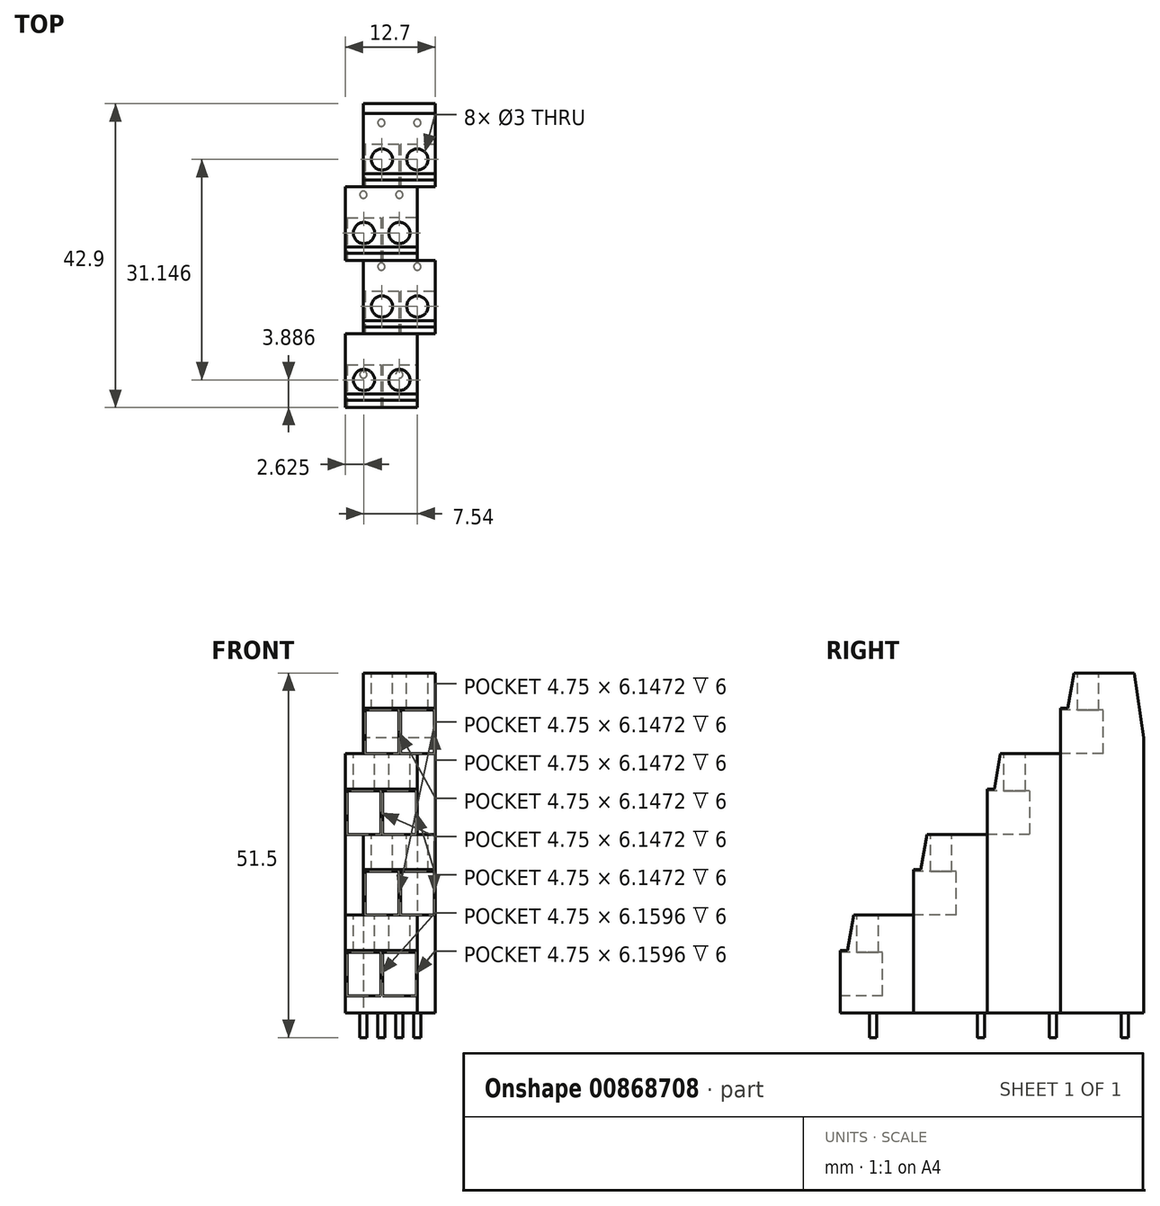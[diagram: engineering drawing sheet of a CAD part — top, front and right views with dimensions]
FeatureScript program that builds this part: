
annotation { "Feature Type Name" : "Feature", "Feature Type Description" : "" }
export const myFeature = defineFeature(function(context is Context, id is Id, definition is map)
    precondition{}
    {
        {
            var Q0;
            Q0=qCreatedBy(makeId("Right.planeOp"),FACE);
            var sketch = newSketch(context, id + "F0", { "sketchPlane" : qUnion([Q0])});
            skLineSegment(sketch, "E0.bottom", {"start": v(1.88, 24.08) * mm, "end": v(10.38, 24.08) * mm});
            skLineSegment(sketch, "E0.top", {"start": v(-31.15, -23.92) * mm, "end": v(11.75, -23.92) * mm});
            skLineSegment(sketch, "E0.left", {"start": v(-31.15, -15.12) * mm, "end": v(-31.15, -23.92) * mm});
            skLineSegment(sketch, "E0.right", {"start": v(11.75, 14.92) * mm, "end": v(11.75, -23.92) * mm});
            skPoint(sketch, "E0.middle", {"position": v(-0.86, 0) * mm});
            skLineSegment(sketch, "E1", {"start": v(-31.15, -15.12) * mm, "end": v(-30.15, -15.12) * mm});
            skLineSegment(sketch, "E2", {"start": v(-30.15, -15.12) * mm, "end": v(-29.26, -10.12) * mm});
            skLineSegment(sketch, "E3", {"start": v(-29.26, -10.12) * mm, "end": v(-20.76, -10.12) * mm});
            skLineSegment(sketch, "E4", {"start": v(-20.76, -10.12) * mm, "end": v(-20.76, -3.72) * mm});
            skLineSegment(sketch, "E5", {"start": v(-20.76, -3.72) * mm, "end": v(-19.76, -3.72) * mm});
            skLineSegment(sketch, "E6", {"start": v(-19.76, -3.72) * mm, "end": v(-18.88, 1.28) * mm});
            skLineSegment(sketch, "E7", {"start": v(-18.88, 1.28) * mm, "end": v(-10.38, 1.28) * mm});
            skLineSegment(sketch, "E8", {"start": v(-10.38, 1.28) * mm, "end": v(-10.38, 7.68) * mm});
            skLineSegment(sketch, "E9", {"start": v(-10.38, 7.68) * mm, "end": v(-9.38, 7.68) * mm});
            skLineSegment(sketch, "E10", {"start": v(-9.38, 7.68) * mm, "end": v(-8.5, 12.68) * mm});
            skLineSegment(sketch, "E11", {"start": v(-8.5, 12.68) * mm, "end": v(0, 12.68) * mm});
            skLineSegment(sketch, "E12", {"start": v(0, 12.68) * mm, "end": v(0, 19.08) * mm});
            skLineSegment(sketch, "E13", {"start": v(0, 19.08) * mm, "end": v(1, 19.08) * mm});
            skLineSegment(sketch, "E14", {"start": v(1, 19.08) * mm, "end": v(1.88, 24.08) * mm});
            skLineSegment(sketch, "E15", {"start": v(10.38, 24.08) * mm, "end": v(11.75, 14.92) * mm});
            skSolve(sketch);
        }
        {
            var Q0;
            Q0=qSketchRegion(id+"F0",true);
            extrude(context, id + "F1", {"entities" : qUnion([Q0]), "endBound" : BoundingType.SYMMETRIC, "depth" : 12.7 * mm, "offsetDistance" : 25.4 * mm});
        }
        {
            var Q0;
            Q0=makeQuery(id+"F1.opExtrude","CAP_FACE",FACE,{"disambiguationData":[OSD([sQuery(id+"F0.wireOp",EDGE,"E0.bottom"),sQuery(id+"F0.wireOp",EDGE,"E0.top"),sQuery(id+"F0.wireOp",EDGE,"E0.left"),sQuery(id+"F0.wireOp",EDGE,"E0.right"),sQuery(id+"F0.wireOp",EDGE,"E1"),sQuery(id+"F0.wireOp",EDGE,"E2"),sQuery(id+"F0.wireOp",EDGE,"E3"),sQuery(id+"F0.wireOp",EDGE,"E4"),sQuery(id+"F0.wireOp",EDGE,"E5"),sQuery(id+"F0.wireOp",EDGE,"E6"),sQuery(id+"F0.wireOp",EDGE,"E7"),sQuery(id+"F0.wireOp",EDGE,"E8"),sQuery(id+"F0.wireOp",EDGE,"E9"),sQuery(id+"F0.wireOp",EDGE,"E10"),sQuery(id+"F0.wireOp",EDGE,"E11"),sQuery(id+"F0.wireOp",EDGE,"E12"),sQuery(id+"F0.wireOp",EDGE,"E13"),sQuery(id+"F0.wireOp",EDGE,"E14"),sQuery(id+"F0.wireOp",EDGE,"E15")])],"isStart":true});
            var sketch = newSketch(context, id + "F2", { "sketchPlane" : qUnion([Q0])});
            skLineSegment(sketch, "E16", {"start": v(20.76, -10.12) * mm, "end": v(20.76, -23.92) * mm});
            skLineSegment(sketch, "E17", {"start": v(0, 12.68) * mm, "end": v(0, -23.92) * mm});
            skLineSegment(sketch, "E18", {"start": v(10.38, 1.28) * mm, "end": v(10.38, -23.92) * mm});
            skSolve(sketch);
        }
        {
            var Q0;
            {var subQ1=sQuery(id+"F2.wireOp",EDGE,"E17");Q0=makeQuery(id+"F2.imprint","IMPRINT",FACE,{"disambiguationData":[TD([[makeQuery(id+"F2.imprint","IMPRINT",EDGE,{"derivedFrom":subQ1}),-1.0]])]});}
            var Q1;
            {var subQ1=sQuery(id+"F2.wireOp",EDGE,"E16");Q1=makeQuery(id+"F2.imprint","IMPRINT",FACE,{"disambiguationData":[TD([[makeQuery(id+"F2.imprint","IMPRINT",EDGE,{"derivedFrom":subQ1}),-1.0]])]});}
            extrude(context, id + "F3", {"entities" : qUnion([Q0, Q1]), "operationType" : NewBodyOperationType.REMOVE, "oppositeDirection" : true, "depth" : 2.54 * mm, "offsetDistance" : 25.4 * mm});
        }
        {
            var Q0;
            Q0=makeQuery(id+"F1.opExtrude","CAP_FACE",FACE,{"disambiguationData":[OSD([sQuery(id+"F0.wireOp",EDGE,"E0.bottom"),sQuery(id+"F0.wireOp",EDGE,"E0.top"),sQuery(id+"F0.wireOp",EDGE,"E0.left"),sQuery(id+"F0.wireOp",EDGE,"E0.right"),sQuery(id+"F0.wireOp",EDGE,"E1"),sQuery(id+"F0.wireOp",EDGE,"E2"),sQuery(id+"F0.wireOp",EDGE,"E3"),sQuery(id+"F0.wireOp",EDGE,"E4"),sQuery(id+"F0.wireOp",EDGE,"E5"),sQuery(id+"F0.wireOp",EDGE,"E6"),sQuery(id+"F0.wireOp",EDGE,"E7"),sQuery(id+"F0.wireOp",EDGE,"E8"),sQuery(id+"F0.wireOp",EDGE,"E9"),sQuery(id+"F0.wireOp",EDGE,"E10"),sQuery(id+"F0.wireOp",EDGE,"E11"),sQuery(id+"F0.wireOp",EDGE,"E12"),sQuery(id+"F0.wireOp",EDGE,"E13"),sQuery(id+"F0.wireOp",EDGE,"E14"),sQuery(id+"F0.wireOp",EDGE,"E15")])],"isStart":false});
            var sketch = newSketch(context, id + "F4", { "sketchPlane" : qUnion([Q0])});
            skLineSegment(sketch, "E19", {"start": v(-20.76, -10.12) * mm, "end": v(-20.76, -23.92) * mm});
            skLineSegment(sketch, "E20", {"start": v(-10.38, 1.28) * mm, "end": v(-10.38, -23.92) * mm});
            skLineSegment(sketch, "E21", {"start": v(0, 12.68) * mm, "end": v(0, -23.92) * mm});
            skSolve(sketch);
        }
        {
            var Q0;
            {var subQ1=sQuery(id+"F4.wireOp",EDGE,"E19");Q0=makeQuery(id+"F4.imprint","IMPRINT",FACE,{"disambiguationData":[TD([[makeQuery(id+"F4.imprint","IMPRINT",EDGE,{"derivedFrom":subQ1}),-1.0]])]});}
            var Q1;
            {var subQ1=sQuery(id+"F4.wireOp",EDGE,"E20");Q1=makeQuery(id+"F4.imprint","IMPRINT",FACE,{"disambiguationData":[TD([[makeQuery(id+"F4.imprint","IMPRINT",EDGE,{"derivedFrom":subQ1}),1.0]])]});}
            extrude(context, id + "F5", {"entities" : qUnion([Q0, Q1]), "operationType" : NewBodyOperationType.REMOVE, "oppositeDirection" : true, "depth" : 2.54 * mm, "offsetDistance" : 25.4 * mm});
        }
        {
            var Q0;
            Q0=makeQuery(id+"F1.opExtrude","SWEPT_FACE",FACE,{"disambiguationData":[OSD([sQuery(id+"F0.wireOp",EDGE,"E0.left")])]});
            var sketch = newSketch(context, id + "F6", { "sketchPlane" : qUnion([Q0])});
            skLineSegment(sketch, "E22.bottom", {"start": v(-6.1, -21.53) * mm, "end": v(-1.35, -21.53) * mm});
            skLineSegment(sketch, "E22.top", {"start": v(-6.1, -15.37) * mm, "end": v(-1.35, -15.37) * mm});
            skLineSegment(sketch, "E22.left", {"start": v(-6.1, -21.53) * mm, "end": v(-6.1, -15.37) * mm});
            skLineSegment(sketch, "E22.right", {"start": v(-1.35, -21.53) * mm, "end": v(-1.35, -15.37) * mm});
            skLineSegment(sketch, "E23.1.0.0", {"start": v(-1.1, -21.53) * mm, "end": v(3.65, -21.53) * mm});
            skLineSegment(sketch, "E23.1.0.1", {"start": v(-1.1, -15.37) * mm, "end": v(3.65, -15.37) * mm});
            skLineSegment(sketch, "E23.1.0.2", {"start": v(3.65, -21.53) * mm, "end": v(3.65, -15.37) * mm});
            skLineSegment(sketch, "E23.1.0.3", {"start": v(-1.1, -21.53) * mm, "end": v(-1.1, -15.37) * mm});
            skLineSegment(sketch, "E23.2.0.0", {"start": v(3.9, -21.53) * mm, "end": v(8.65, -21.53) * mm});
            skLineSegment(sketch, "E23.2.0.1", {"start": v(3.9, -15.37) * mm, "end": v(8.65, -15.37) * mm});
            skLineSegment(sketch, "E23.2.0.2", {"start": v(8.65, -21.53) * mm, "end": v(8.65, -15.37) * mm});
            skLineSegment(sketch, "E23.2.0.3", {"start": v(3.9, -21.53) * mm, "end": v(3.9, -15.37) * mm});
            skLineSegment(sketch, "E23.direction1", {"start": v(-6.1, -21.53) * mm, "end": v(-1.1, -21.53) * mm, "construction": true});
            skSolve(sketch);
        }
        {
            var Q0;
            Q0=makeQuery(id+"F5.boolean.opBoolean","MERGE",FACE,{"derivedFrom":[makeQuery(id+"F1.opExtrude","SWEPT_FACE",FACE,{"disambiguationData":[OSD([sQuery(id+"F0.wireOp",EDGE,"E4")])]})],"fromTools":[makeQuery(id+"F5.opExtrude","SWEPT_FACE",FACE,{"disambiguationData":[OSD([sQuery(id+"F4.wireOp",EDGE,"E19")])]})]});
            var sketch = newSketch(context, id + "F7", { "sketchPlane" : qUnion([Q0])});
            skLineSegment(sketch, "E24.bottom", {"start": v(-3.56, -10.12) * mm, "end": v(1.2, -10.12) * mm});
            skLineSegment(sketch, "E24.top", {"start": v(-3.56, -3.97) * mm, "end": v(1.19, -3.97) * mm});
            skLineSegment(sketch, "E24.left", {"start": v(-3.56, -10.12) * mm, "end": v(-3.56, -3.97) * mm});
            skLineSegment(sketch, "E24.right", {"start": v(1.2, -10.12) * mm, "end": v(1.19, -3.97) * mm});
            skLineSegment(sketch, "E25.1.0.0", {"start": v(1.44, -10.12) * mm, "end": v(1.44, -3.97) * mm});
            skLineSegment(sketch, "E25.1.0.1", {"start": v(1.44, -3.97) * mm, "end": v(6.19, -3.97) * mm});
            skLineSegment(sketch, "E25.1.0.2", {"start": v(6.2, -10.12) * mm, "end": v(6.19, -3.97) * mm});
            skLineSegment(sketch, "E25.1.0.3", {"start": v(1.44, -10.12) * mm, "end": v(6.2, -10.12) * mm});
            skLineSegment(sketch, "E25.2.0.0", {"start": v(6.44, -10.12) * mm, "end": v(6.44, -3.97) * mm});
            skLineSegment(sketch, "E25.2.0.1", {"start": v(6.44, -3.97) * mm, "end": v(11.19, -3.97) * mm});
            skLineSegment(sketch, "E25.2.0.2", {"start": v(11.2, -10.12) * mm, "end": v(11.19, -3.97) * mm});
            skLineSegment(sketch, "E25.2.0.3", {"start": v(6.44, -10.12) * mm, "end": v(11.2, -10.12) * mm});
            skLineSegment(sketch, "E25.direction1", {"start": v(-3.56, -10.12) * mm, "end": v(1.44, -10.12) * mm, "construction": true});
            skSolve(sketch);
        }
        {
            var Q0;
            Q0=makeQuery(id+"F1.opExtrude","SWEPT_FACE",FACE,{"disambiguationData":[OSD([sQuery(id+"F0.wireOp",EDGE,"E8")])]});
            var sketch = newSketch(context, id + "F8", { "sketchPlane" : qUnion([Q0])});
            skLineSegment(sketch, "E26.bottom", {"start": v(-6.1, 1.28) * mm, "end": v(-1.35, 1.28) * mm});
            skLineSegment(sketch, "E26.top", {"start": v(-6.1, 7.43) * mm, "end": v(-1.35, 7.43) * mm});
            skLineSegment(sketch, "E26.left", {"start": v(-1.35, 7.43) * mm, "end": v(-1.35, 1.28) * mm});
            skLineSegment(sketch, "E26.right", {"start": v(-6.1, 7.43) * mm, "end": v(-6.1, 1.28) * mm});
            skLineSegment(sketch, "E27.1.0.0", {"start": v(-1.1, 1.28) * mm, "end": v(3.65, 1.28) * mm});
            skLineSegment(sketch, "E27.1.0.1", {"start": v(3.65, 7.43) * mm, "end": v(3.65, 1.28) * mm});
            skLineSegment(sketch, "E27.1.0.2", {"start": v(-1.1, 7.43) * mm, "end": v(-1.1, 1.28) * mm});
            skLineSegment(sketch, "E27.1.0.3", {"start": v(-1.1, 7.43) * mm, "end": v(3.65, 7.43) * mm});
            skLineSegment(sketch, "E27.2.0.0", {"start": v(3.9, 1.28) * mm, "end": v(8.65, 1.28) * mm});
            skLineSegment(sketch, "E27.2.0.1", {"start": v(8.65, 7.43) * mm, "end": v(8.65, 1.28) * mm});
            skLineSegment(sketch, "E27.2.0.2", {"start": v(3.9, 7.43) * mm, "end": v(3.9, 1.28) * mm});
            skLineSegment(sketch, "E27.2.0.3", {"start": v(3.9, 7.43) * mm, "end": v(8.65, 7.43) * mm});
            skLineSegment(sketch, "E27.direction1", {"start": v(-1.35, 1.28) * mm, "end": v(3.65, 1.28) * mm, "construction": true});
            skSolve(sketch);
        }
        {
            var Q0;
            Q0=makeQuery(id+"F5.boolean.opBoolean","MERGE",FACE,{"derivedFrom":[makeQuery(id+"F1.opExtrude","SWEPT_FACE",FACE,{"disambiguationData":[OSD([sQuery(id+"F0.wireOp",EDGE,"E12")])]})],"fromTools":[makeQuery(id+"F5.opExtrude","SWEPT_FACE",FACE,{"disambiguationData":[OSD([sQuery(id+"F4.wireOp",EDGE,"E21")])]})]});
            var sketch = newSketch(context, id + "F9", { "sketchPlane" : qUnion([Q0])});
            skLineSegment(sketch, "E28.bottom", {"start": v(-3.56, 12.68) * mm, "end": v(1.2, 12.68) * mm});
            skLineSegment(sketch, "E28.top", {"start": v(-3.56, 18.83) * mm, "end": v(1.19, 18.83) * mm});
            skLineSegment(sketch, "E28.left", {"start": v(-3.56, 12.68) * mm, "end": v(-3.56, 18.83) * mm});
            skLineSegment(sketch, "E28.right", {"start": v(1.2, 12.68) * mm, "end": v(1.19, 18.83) * mm});
            skLineSegment(sketch, "E29.1.0.0", {"start": v(1.44, 12.68) * mm, "end": v(6.2, 12.68) * mm});
            skLineSegment(sketch, "E29.1.0.1", {"start": v(1.44, 18.83) * mm, "end": v(6.19, 18.83) * mm});
            skLineSegment(sketch, "E29.1.0.2", {"start": v(6.2, 12.68) * mm, "end": v(6.19, 18.83) * mm});
            skLineSegment(sketch, "E29.1.0.3", {"start": v(1.44, 12.68) * mm, "end": v(1.44, 18.83) * mm});
            skLineSegment(sketch, "E29.2.0.0", {"start": v(6.44, 12.68) * mm, "end": v(11.2, 12.68) * mm});
            skLineSegment(sketch, "E29.2.0.1", {"start": v(6.44, 18.83) * mm, "end": v(11.19, 18.83) * mm});
            skLineSegment(sketch, "E29.2.0.2", {"start": v(11.2, 12.68) * mm, "end": v(11.19, 18.83) * mm});
            skLineSegment(sketch, "E29.2.0.3", {"start": v(6.44, 12.68) * mm, "end": v(6.44, 18.83) * mm});
            skLineSegment(sketch, "E29.direction1", {"start": v(-3.56, 12.68) * mm, "end": v(1.44, 12.68) * mm, "construction": true});
            skSolve(sketch);
        }
        {
            var Q0;
            Q0=makeQuery(id+"F6.imprint","IMPRINT",FACE,{"disambiguationData":[TD([[makeQuery(id+"F6.imprint","IMPRINT",EDGE,{"derivedFrom":sQuery(id+"F6.wireOp",EDGE,"E22.bottom")}),1.0]])]});
            var Q1;
            Q1=makeQuery(id+"F6.imprint","IMPRINT",FACE,{"disambiguationData":[TD([[makeQuery(id+"F6.imprint","IMPRINT",EDGE,{"derivedFrom":sQuery(id+"F6.wireOp",EDGE,"E23.1.0.0")}),1.0]])]});
            var Q2;
            Q2=makeQuery(id+"F6.imprint","IMPRINT",FACE,{"disambiguationData":[TD([[makeQuery(id+"F6.imprint","IMPRINT",EDGE,{"derivedFrom":sQuery(id+"F6.wireOp",EDGE,"E23.2.0.0")}),1.0]])]});
            var Q3;
            Q3=makeQuery(id+"F8.imprint","IMPRINT",FACE,{"disambiguationData":[TD([[makeQuery(id+"F8.imprint","IMPRINT",EDGE,{"derivedFrom":sQuery(id+"F8.wireOp",EDGE,"E26.top")}),-1.0]])]});
            var Q4;
            Q4=makeQuery(id+"F8.imprint","IMPRINT",FACE,{"disambiguationData":[TD([[makeQuery(id+"F8.imprint","IMPRINT",EDGE,{"derivedFrom":sQuery(id+"F8.wireOp",EDGE,"E27.1.0.0")}),-1.0]])]});
            var Q5;
            Q5=makeQuery(id+"F8.imprint","IMPRINT",FACE,{"disambiguationData":[TD([[makeQuery(id+"F8.imprint","IMPRINT",EDGE,{"derivedFrom":sQuery(id+"F8.wireOp",EDGE,"E27.2.0.0")}),-1.0]])]});
            var Q6;
            Q6=makeQuery(id+"F7.imprint","IMPRINT",FACE,{"disambiguationData":[TD([[makeQuery(id+"F7.imprint","IMPRINT",EDGE,{"derivedFrom":sQuery(id+"F7.wireOp",EDGE,"E24.bottom")}),-1.0]])]});
            var Q7;
            Q7=makeQuery(id+"F9.imprint","IMPRINT",FACE,{"disambiguationData":[TD([[makeQuery(id+"F9.imprint","IMPRINT",EDGE,{"derivedFrom":sQuery(id+"F9.wireOp",EDGE,"E28.bottom")}),-1.0]])]});
            var Q8;
            Q8=makeQuery(id+"F9.imprint","IMPRINT",FACE,{"disambiguationData":[TD([[makeQuery(id+"F9.imprint","IMPRINT",EDGE,{"derivedFrom":sQuery(id+"F9.wireOp",EDGE,"E29.1.0.0")}),-1.0]])]});
            var Q9;
            Q9=makeQuery(id+"F9.imprint","IMPRINT",FACE,{"disambiguationData":[TD([[makeQuery(id+"F9.imprint","IMPRINT",EDGE,{"derivedFrom":sQuery(id+"F9.wireOp",EDGE,"E29.2.0.1")}),-1.0]])]});
            var Q10;
            Q10=makeQuery(id+"F7.imprint","IMPRINT",FACE,{"disambiguationData":[TD([[makeQuery(id+"F7.imprint","IMPRINT",EDGE,{"derivedFrom":sQuery(id+"F7.wireOp",EDGE,"E25.1.0.0")}),-1.0]])]});
            var Q11;
            {var subQ3=sQuery(id+"F7.wireOp",EDGE,"E25.2.0.0");Q11=makeQuery(id+"F7.imprint","IMPRINT",FACE,{"disambiguationData":[TD([[makeQuery(id+"F7.imprint","IMPRINT",EDGE,{"derivedFrom":subQ3}),-1.0]])]});}
            extrude(context, id + "F10", {"entities" : qUnion([Q0, Q1, Q2, Q3, Q4, Q5, Q6, Q7, Q8, Q9, Q10, Q11]), "operationType" : NewBodyOperationType.REMOVE, "oppositeDirection" : true, "depth" : 6 * mm, "offsetDistance" : 25.4 * mm});
        }
        {
            var Q0;
            Q0=makeQuery(id+"FIPQeaOd7nqBqoZ_1.boolean.opBoolean","MERGE",FACE,{"derivedFrom":[makeQuery(id+"F1.opExtrude","SWEPT_FACE",FACE,{"disambiguationData":[OSD([sQuery(id+"F0.wireOp",EDGE,"E3")])]})],"fromTools":[makeQuery(id+"FIPQeaOd7nqBqoZ_1.opExtrude","SWEPT_FACE",FACE,{"disambiguationData":[OSD([sQuery(id+"FcPPGYhQoeAlAkm_1.wireOp",EDGE,"nRc5gezO-lLlT-aTDT-U5ua-d5aH2JDgAWAg.bottom")])]}),makeQuery(id+"FIPQeaOd7nqBqoZ_1.opExtrude","SWEPT_FACE",FACE,{"disambiguationData":[OSD([sQuery(id+"FcPPGYhQoeAlAkm_1.wireOp",EDGE,"76d76378-90c5-41d6-9edd-ee122aa212bd.1.0.1")])]}),makeQuery(id+"FIPQeaOd7nqBqoZ_1.opExtrude","SWEPT_FACE",FACE,{"disambiguationData":[OSD([sQuery(id+"FcPPGYhQoeAlAkm_1.wireOp",EDGE,"76d76378-90c5-41d6-9edd-ee122aa212bd.2.0.1")])]})]});
            var sketch = newSketch(context, id + "F11", { "sketchPlane" : qUnion([Q0])});
            skCircle(sketch, "E30", {"center": v(-3.72, -27.26) * mm, "radius": 1.5 * mm});
            skCircle(sketch, "E31.1.0.0", {"center": v(1.28, -27.26) * mm, "radius": 1.5 * mm});
            skCircle(sketch, "E31.2.0.0", {"center": v(6.28, -27.26) * mm, "radius": 1.5 * mm});
            skLineSegment(sketch, "E31.direction1", {"start": v(-3.72, -27.26) * mm, "end": v(1.28, -27.26) * mm, "construction": true});
            skSolve(sketch);
        }
        {
            var Q0;
            Q0=makeQuery(id+"FhxDgFylUnVdEJf_1.boolean.opBoolean","MERGE",FACE,{"derivedFrom":[makeQuery(id+"F1.opExtrude","SWEPT_FACE",FACE,{"disambiguationData":[OSD([sQuery(id+"F0.wireOp",EDGE,"E7")])]})],"fromTools":[makeQuery(id+"FhxDgFylUnVdEJf_1.opExtrude","SWEPT_FACE",FACE,{"disambiguationData":[OSD([sQuery(id+"F8.wireOp",EDGE,"E26.bottom")])]}),makeQuery(id+"FhxDgFylUnVdEJf_1.opExtrude","SWEPT_FACE",FACE,{"disambiguationData":[OSD([sQuery(id+"F8.wireOp",EDGE,"E27.1.0.0")])]}),makeQuery(id+"FhxDgFylUnVdEJf_1.opExtrude","SWEPT_FACE",FACE,{"disambiguationData":[OSD([sQuery(id+"F8.wireOp",EDGE,"E27.2.0.0")])]})]});
            var sketch = newSketch(context, id + "F12", { "sketchPlane" : qUnion([Q0])});
            skCircle(sketch, "E32", {"center": v(-1.18, -16.88) * mm, "radius": 1.5 * mm});
            skCircle(sketch, "E33.1.0.0", {"center": v(3.82, -16.88) * mm, "radius": 1.5 * mm});
            skCircle(sketch, "E33.2.0.0", {"center": v(8.81, -16.88) * mm, "radius": 1.5 * mm});
            skLineSegment(sketch, "E33.direction1", {"start": v(-1.18, -16.88) * mm, "end": v(3.82, -16.88) * mm, "construction": true});
            skSolve(sketch);
        }
        {
            var Q0;
            Q0=makeQuery(id+"FWjFDDOlSrOGeWe_1.boolean.opBoolean","MERGE",FACE,{"derivedFrom":[makeQuery(id+"F1.opExtrude","SWEPT_FACE",FACE,{"disambiguationData":[OSD([sQuery(id+"F0.wireOp",EDGE,"E11")])]})],"fromTools":[makeQuery(id+"FWjFDDOlSrOGeWe_1.opExtrude","SWEPT_FACE",FACE,{"disambiguationData":[OSD([sQuery(id+"FboXLxqLQ1Lzw5p_1.wireOp",EDGE,"Zzgv8rQs-4HYb-RqgK-dbSt-XDPfarDPM1yx.bottom")])]}),makeQuery(id+"FWjFDDOlSrOGeWe_1.opExtrude","SWEPT_FACE",FACE,{"disambiguationData":[OSD([sQuery(id+"FboXLxqLQ1Lzw5p_1.wireOp",EDGE,"14db3bff-85f1-4a68-9081-9ea7ad831f3b.1.0.1")])]}),makeQuery(id+"FWjFDDOlSrOGeWe_1.opExtrude","SWEPT_FACE",FACE,{"disambiguationData":[OSD([sQuery(id+"FboXLxqLQ1Lzw5p_1.wireOp",EDGE,"14db3bff-85f1-4a68-9081-9ea7ad831f3b.2.0.1")])]})]});
            var sketch = newSketch(context, id + "F13", { "sketchPlane" : qUnion([Q0])});
            skCircle(sketch, "E34", {"center": v(-3.72, -6.5) * mm, "radius": 1.5 * mm});
            skCircle(sketch, "E35.1.0.0", {"center": v(1.28, -6.5) * mm, "radius": 1.5 * mm});
            skCircle(sketch, "E35.2.0.0", {"center": v(6.28, -6.5) * mm, "radius": 1.5 * mm});
            skLineSegment(sketch, "E35.direction1", {"start": v(-3.72, -6.5) * mm, "end": v(1.28, -6.5) * mm, "construction": true});
            skSolve(sketch);
        }
        {
            var Q0;
            Q0=makeQuery(id+"F1.opExtrude","SWEPT_FACE",FACE,{"disambiguationData":[OSD([sQuery(id+"F0.wireOp",EDGE,"E0.bottom")])]});
            var sketch = newSketch(context, id + "F14", { "sketchPlane" : qUnion([Q0])});
            skCircle(sketch, "E36", {"center": v(-1.18, 3.88) * mm, "radius": 1.5 * mm});
            skCircle(sketch, "E37.1.0.0", {"center": v(3.82, 3.88) * mm, "radius": 1.5 * mm});
            skCircle(sketch, "E37.2.0.0", {"center": v(8.81, 3.88) * mm, "radius": 1.5 * mm});
            skLineSegment(sketch, "E37.direction1", {"start": v(-1.18, 3.88) * mm, "end": v(3.82, 3.88) * mm, "construction": true});
            skSolve(sketch);
        }
        {
            var Q0;
            Q0=makeQuery(id+"F11.imprint","IMPRINT",FACE,{"disambiguationData":[TD([[makeQuery(id+"F11.imprint","IMPRINT",EDGE,{"derivedFrom":sQuery(id+"F11.wireOp",EDGE,"E30")}),1.0]])]});
            var Q1;
            Q1=makeQuery(id+"F11.imprint","IMPRINT",FACE,{"disambiguationData":[TD([[makeQuery(id+"F11.imprint","IMPRINT",EDGE,{"derivedFrom":sQuery(id+"F11.wireOp",EDGE,"E31.1.0.0")}),1.0]])]});
            var Q2;
            Q2=makeQuery(id+"F11.imprint","IMPRINT",FACE,{"disambiguationData":[TD([[makeQuery(id+"F11.imprint","IMPRINT",EDGE,{"derivedFrom":sQuery(id+"F11.wireOp",EDGE,"E31.2.0.0")}),1.0]])]});
            var Q3;
            Q3=makeQuery(id+"F12.imprint","IMPRINT",FACE,{"disambiguationData":[TD([[makeQuery(id+"F12.imprint","IMPRINT",EDGE,{"derivedFrom":sQuery(id+"F12.wireOp",EDGE,"E32")}),1.0]])]});
            var Q4;
            Q4=makeQuery(id+"F12.imprint","IMPRINT",FACE,{"disambiguationData":[TD([[makeQuery(id+"F12.imprint","IMPRINT",EDGE,{"derivedFrom":sQuery(id+"F12.wireOp",EDGE,"E33.1.0.0")}),1.0]])]});
            var Q5;
            Q5=makeQuery(id+"F12.imprint","IMPRINT",FACE,{"disambiguationData":[TD([[makeQuery(id+"F12.imprint","IMPRINT",EDGE,{"derivedFrom":sQuery(id+"F12.wireOp",EDGE,"E33.2.0.0")}),1.0]])]});
            var Q6;
            Q6=makeQuery(id+"F13.imprint","IMPRINT",FACE,{"disambiguationData":[TD([[makeQuery(id+"F13.imprint","IMPRINT",EDGE,{"derivedFrom":sQuery(id+"F13.wireOp",EDGE,"E34")}),1.0]])]});
            var Q7;
            Q7=makeQuery(id+"F13.imprint","IMPRINT",FACE,{"disambiguationData":[TD([[makeQuery(id+"F13.imprint","IMPRINT",EDGE,{"derivedFrom":sQuery(id+"F13.wireOp",EDGE,"E35.1.0.0")}),1.0]])]});
            var Q8;
            Q8=makeQuery(id+"F13.imprint","IMPRINT",FACE,{"disambiguationData":[TD([[makeQuery(id+"F13.imprint","IMPRINT",EDGE,{"derivedFrom":sQuery(id+"F13.wireOp",EDGE,"E35.2.0.0")}),1.0]])]});
            var Q9;
            Q9=makeQuery(id+"F14.imprint","IMPRINT",FACE,{"disambiguationData":[TD([[makeQuery(id+"F14.imprint","IMPRINT",EDGE,{"derivedFrom":sQuery(id+"F14.wireOp",EDGE,"E36")}),1.0]])]});
            var Q10;
            Q10=makeQuery(id+"F14.imprint","IMPRINT",FACE,{"disambiguationData":[TD([[makeQuery(id+"F14.imprint","IMPRINT",EDGE,{"derivedFrom":sQuery(id+"F14.wireOp",EDGE,"E37.1.0.0")}),1.0]])]});
            var Q11;
            Q11=makeQuery(id+"F14.imprint","IMPRINT",FACE,{"disambiguationData":[TD([[makeQuery(id+"F14.imprint","IMPRINT",EDGE,{"derivedFrom":sQuery(id+"F14.wireOp",EDGE,"E37.2.0.0")}),1.0]])]});
            extrude(context, id + "F15", {"entities" : qUnion([Q0, Q1, Q2, Q3, Q4, Q5, Q6, Q7, Q8, Q9, Q10, Q11]), "operationType" : NewBodyOperationType.REMOVE, "oppositeDirection" : true, "depth" : 6 * mm, "offsetDistance" : 25.4 * mm});
        }
        {
            var Q0;
            Q0=makeQuery(id+"F1.opExtrude","SWEPT_FACE",FACE,{"disambiguationData":[OSD([sQuery(id+"F0.wireOp",EDGE,"E0.top")])]});
            var sketch = newSketch(context, id + "F16", { "sketchPlane" : qUnion([Q0])});
            skCircle(sketch, "E38", {"center": v(1.27, 26.5) * mm, "radius": 0.5 * mm});
            skCircle(sketch, "E39.1.0.0", {"center": v(-3.81, 26.5) * mm, "radius": 0.5 * mm});
            skLineSegment(sketch, "E39.direction1", {"start": v(1.27, 26.5) * mm, "end": v(-3.81, 26.5) * mm, "construction": true});
            skCircle(sketch, "E40", {"center": v(1.27, 1.1) * mm, "radius": 0.5 * mm});
            skCircle(sketch, "E41.1.0.0", {"center": v(-3.8, 1.1) * mm, "radius": 0.5 * mm});
            skLineSegment(sketch, "E41.direction1", {"start": v(1.27, 1.1) * mm, "end": v(-3.8, 1.1) * mm, "construction": true});
            skCircle(sketch, "E42", {"center": v(3.8, 11.26) * mm, "radius": 0.5 * mm});
            skCircle(sketch, "E43.1.0.0", {"center": v(-1.27, 11.26) * mm, "radius": 0.5 * mm});
            skLineSegment(sketch, "E43.direction1", {"start": v(3.8, 11.26) * mm, "end": v(-1.27, 11.26) * mm, "construction": true});
            skCircle(sketch, "E44", {"center": v(3.8, -9.06) * mm, "radius": 0.5 * mm});
            skCircle(sketch, "E45.1.0.0", {"center": v(-1.27, -9.06) * mm, "radius": 0.5 * mm});
            skLineSegment(sketch, "E45.direction1", {"start": v(3.8, -9.06) * mm, "end": v(-1.27, -9.06) * mm, "construction": true});
            skSolve(sketch);
        }
        {
            var Q0;
            Q0=makeQuery(id+"F16.imprint","IMPRINT",FACE,{"disambiguationData":[TD([[makeQuery(id+"F16.imprint","IMPRINT",EDGE,{"derivedFrom":sQuery(id+"F16.wireOp",EDGE,"E38")}),1.0]])]});
            var Q1;
            Q1=makeQuery(id+"F16.imprint","IMPRINT",FACE,{"disambiguationData":[TD([[makeQuery(id+"F16.imprint","IMPRINT",EDGE,{"derivedFrom":sQuery(id+"F16.wireOp",EDGE,"E39.1.0.0")}),1.0]])]});
            var Q2;
            Q2=makeQuery(id+"F16.imprint","IMPRINT",FACE,{"disambiguationData":[TD([[makeQuery(id+"F16.imprint","IMPRINT",EDGE,{"derivedFrom":sQuery(id+"F16.wireOp",EDGE,"E39.2.0.0")}),1.0]])]});
            var Q3;
            Q3=makeQuery(id+"F16.imprint","IMPRINT",FACE,{"disambiguationData":[TD([[makeQuery(id+"F16.imprint","IMPRINT",EDGE,{"derivedFrom":sQuery(id+"F16.wireOp",EDGE,"E42")}),1.0]])]});
            var Q4;
            Q4=makeQuery(id+"F16.imprint","IMPRINT",FACE,{"disambiguationData":[TD([[makeQuery(id+"F16.imprint","IMPRINT",EDGE,{"derivedFrom":sQuery(id+"F16.wireOp",EDGE,"E43.1.0.0")}),1.0]])]});
            var Q5;
            Q5=makeQuery(id+"F16.imprint","IMPRINT",FACE,{"disambiguationData":[TD([[makeQuery(id+"F16.imprint","IMPRINT",EDGE,{"derivedFrom":sQuery(id+"F16.wireOp",EDGE,"E43.2.0.0")}),1.0]])]});
            var Q6;
            Q6=makeQuery(id+"F16.imprint","IMPRINT",FACE,{"disambiguationData":[TD([[makeQuery(id+"F16.imprint","IMPRINT",EDGE,{"derivedFrom":sQuery(id+"F16.wireOp",EDGE,"E41.2.0.0")}),1.0]])]});
            var Q7;
            Q7=makeQuery(id+"F16.imprint","IMPRINT",FACE,{"disambiguationData":[TD([[makeQuery(id+"F16.imprint","IMPRINT",EDGE,{"derivedFrom":sQuery(id+"F16.wireOp",EDGE,"E41.1.0.0")}),1.0]])]});
            var Q8;
            Q8=makeQuery(id+"F16.imprint","IMPRINT",FACE,{"disambiguationData":[TD([[makeQuery(id+"F16.imprint","IMPRINT",EDGE,{"derivedFrom":sQuery(id+"F16.wireOp",EDGE,"E40")}),1.0]])]});
            var Q9;
            Q9=makeQuery(id+"F16.imprint","IMPRINT",FACE,{"disambiguationData":[TD([[makeQuery(id+"F16.imprint","IMPRINT",EDGE,{"derivedFrom":sQuery(id+"F16.wireOp",EDGE,"E44")}),1.0]])]});
            var Q10;
            Q10=makeQuery(id+"F16.imprint","IMPRINT",FACE,{"disambiguationData":[TD([[makeQuery(id+"F16.imprint","IMPRINT",EDGE,{"derivedFrom":sQuery(id+"F16.wireOp",EDGE,"E45.1.0.0")}),1.0]])]});
            var Q11;
            Q11=makeQuery(id+"F16.imprint","IMPRINT",FACE,{"disambiguationData":[TD([[makeQuery(id+"F16.imprint","IMPRINT",EDGE,{"derivedFrom":sQuery(id+"F16.wireOp",EDGE,"E45.2.0.0")}),1.0]])]});
            extrude(context, id + "F17", {"entities" : qUnion([Q0, Q1, Q2, Q3, Q4, Q5, Q6, Q7, Q8, Q9, Q10, Q11]), "operationType" : NewBodyOperationType.ADD, "depth" : 3.5 * mm, "offsetDistance" : 25.4 * mm});
        }
    });
